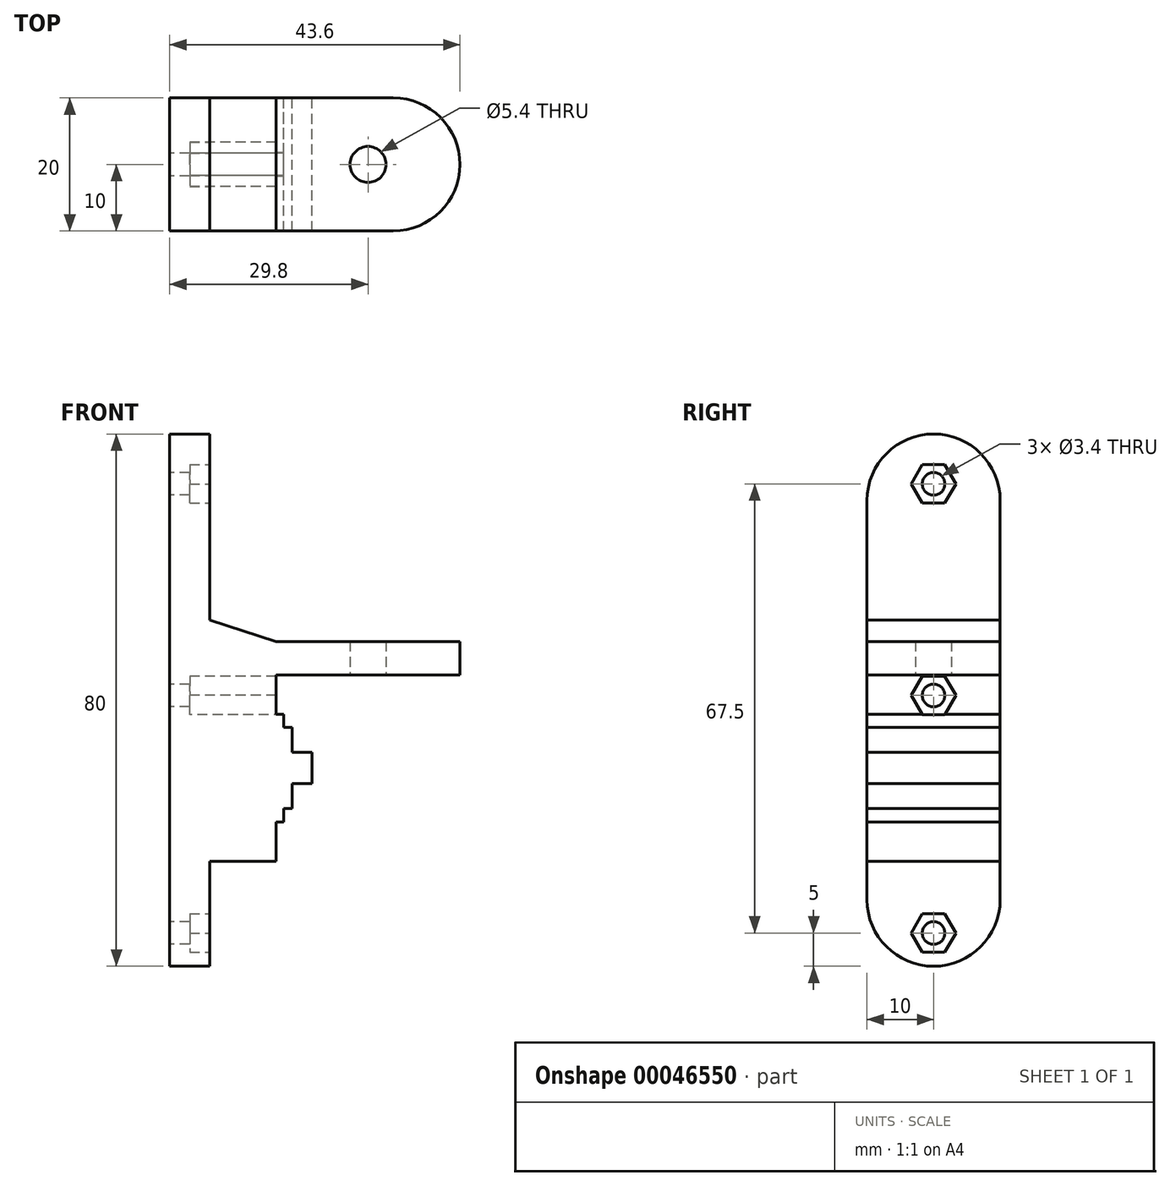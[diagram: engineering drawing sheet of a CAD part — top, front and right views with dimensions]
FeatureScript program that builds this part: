
annotation { "Feature Type Name" : "Feature", "Feature Type Description" : "" }
export const myFeature = defineFeature(function(context is Context, id is Id, definition is map)
    precondition{}
    {
        {
            var Q0;
            Q0=qCreatedBy(makeId("Front.planeOp"),FACE);
            var sketch = newSketch(context, id + "F0", { "sketchPlane" : qUnion([Q0])});
            skLineSegment(sketch, "E0", {"start": v(6, 12) * mm, "end": v(16, 8.8) * mm});
            skLineSegment(sketch, "E1", {"start": v(16, 8.8) * mm, "end": v(43.6, 8.8) * mm});
            skLineSegment(sketch, "E2", {"start": v(43.6, 8.8) * mm, "end": v(43.6, 3.8) * mm});
            skLineSegment(sketch, "E3", {"start": v(43.6, 3.8) * mm, "end": v(16, 3.8) * mm});
            skLineSegment(sketch, "E4", {"start": v(16, 3.8) * mm, "end": v(16, -2.1) * mm});
            skLineSegment(sketch, "E5", {"start": v(16, -2.1) * mm, "end": v(17.15, -2.1) * mm});
            skLineSegment(sketch, "E6", {"start": v(17.15, -2.1) * mm, "end": v(17.15, -4.1) * mm});
            skLineSegment(sketch, "E7", {"start": v(17.15, -4.1) * mm, "end": v(18.4, -4.1) * mm});
            skLineSegment(sketch, "E8", {"start": v(18.4, -4.1) * mm, "end": v(18.4, -7.85) * mm});
            skLineSegment(sketch, "E9", {"start": v(18.4, -7.85) * mm, "end": v(21.4, -7.85) * mm});
            skLineSegment(sketch, "E10", {"start": v(21.4, -7.85) * mm, "end": v(21.4, -12.55) * mm});
            skLineSegment(sketch, "E11", {"start": v(21.4, -12.55) * mm, "end": v(18.4, -12.55) * mm});
            skLineSegment(sketch, "E12", {"start": v(18.4, -12.55) * mm, "end": v(18.4, -16.3) * mm});
            skLineSegment(sketch, "E13", {"start": v(18.4, -16.3) * mm, "end": v(17.15, -16.3) * mm});
            skLineSegment(sketch, "E14", {"start": v(17.15, -16.3) * mm, "end": v(17.15, -18.3) * mm});
            skLineSegment(sketch, "E15", {"start": v(17.15, -18.3) * mm, "end": v(16, -18.3) * mm});
            skLineSegment(sketch, "E16", {"start": v(16, -18.3) * mm, "end": v(16, -24.2) * mm});
            skLineSegment(sketch, "E17", {"start": v(16, -24.2) * mm, "end": v(6, -24.2) * mm});
            skLineSegment(sketch, "E18", {"start": v(0, 40) * mm, "end": v(6, 40) * mm});
            skLineSegment(sketch, "E19", {"start": v(0, -40) * mm, "end": v(6, -40) * mm});
            skLineSegment(sketch, "E20", {"start": v(6, -40) * mm, "end": v(6, -24.2) * mm});
            skLineSegment(sketch, "E21", {"start": v(0, 40) * mm, "end": v(0, -40) * mm});
            skLineSegment(sketch, "E22", {"start": v(6, 40) * mm, "end": v(6, 12) * mm});
            skLineSegment(sketch, "E23", {"start": v(16, 8.8) * mm, "end": v(16, -24.2) * mm, "construction": true});
            skSolve(sketch);
        }
        {
            var Q0;
            Q0=qSketchRegion(id+"F0",true);
            extrude(context, id + "F1", {"entities" : qUnion([Q0]), "depth" : 20 * mm});
        }
        {
            var Q0;
            Q0=makeQuery(id+"F1.opExtrude","SWEPT_FACE",FACE,{"disambiguationData":[OSD([sQuery(id+"F0.wireOp",EDGE,"E3")])]});
            var sketch = newSketch(context, id + "F2", { "sketchPlane" : qUnion([Q0])});
            skLineSegment(sketch, "E24", {"start": v(43.6, 10) * mm, "end": v(16, 10) * mm, "construction": true});
            skLineSegment(sketch, "E25", {"start": v(29.8, 20) * mm, "end": v(29.8, 0) * mm, "construction": true});
            skCircle(sketch, "E26", {"center": v(29.8, 10) * mm, "radius": 2.7 * mm});
            skSolve(sketch);
        }
        {
            var Q0;
            Q0=makeQuery(id+"F2.imprint","IMPRINT",FACE,{"disambiguationData":[TD([[makeQuery(id+"F2.imprint","IMPRINT",EDGE,{"derivedFrom":sQuery(id+"F2.wireOp",EDGE,"E26")}),1.0]])]});
            var Q1;
            Q1=sQuery(id+"F2.wireOp",EDGE,"E26");
            extrude(context, id + "F3", {"entities" : qUnion([Q0]), "operationType" : NewBodyOperationType.REMOVE, "surfaceEntities" : qUnion([Q1]), "endBound" : BoundingType.UP_TO_NEXT, "oppositeDirection" : true, "depth" : 25 * mm});
        }
        {
            var Q0;
            Q0=makeQuery(id+"F1.opExtrude","SWEPT_FACE",FACE,{"disambiguationData":[OSD([sQuery(id+"F0.wireOp",EDGE,"E21")])]});
            var sketch = newSketch(context, id + "F4", { "sketchPlane" : qUnion([Q0])});
            skCircle(sketch, "E27", {"center": v(10, 32.5) * mm, "radius": 1.7 * mm});
            skCircle(sketch, "E28", {"center": v(10, 0.7) * mm, "radius": 1.7 * mm});
            skCircle(sketch, "E29", {"center": v(10, -35) * mm, "radius": 1.7 * mm});
            skLineSegment(sketch, "E30", {"start": v(10, 40) * mm, "end": v(10, -40) * mm, "construction": true});
            skSolve(sketch);
        }
        {
            var Q0;
            Q0=makeQuery(id+"F4.imprint","IMPRINT",FACE,{"disambiguationData":[TD([[makeQuery(id+"F4.imprint","IMPRINT",EDGE,{"derivedFrom":sQuery(id+"F4.wireOp",EDGE,"E27")}),1.0]])]});
            var Q1;
            Q1=makeQuery(id+"F4.imprint","IMPRINT",FACE,{"disambiguationData":[TD([[makeQuery(id+"F4.imprint","IMPRINT",EDGE,{"derivedFrom":sQuery(id+"F4.wireOp",EDGE,"E28")}),1.0]])]});
            var Q2;
            Q2=makeQuery(id+"F4.imprint","IMPRINT",FACE,{"disambiguationData":[TD([[makeQuery(id+"F4.imprint","IMPRINT",EDGE,{"derivedFrom":sQuery(id+"F4.wireOp",EDGE,"E29")}),1.0]])]});
            extrude(context, id + "F5", {"entities" : qUnion([Q0, Q1, Q2]), "operationType" : NewBodyOperationType.REMOVE, "endBound" : BoundingType.UP_TO_NEXT, "oppositeDirection" : true, "depth" : 25 * mm});
        }
        {
            var Q0;
            Q0=makeQuery(id+"F1.opExtrude","SWEPT_FACE",FACE,{"disambiguationData":[OSD([sQuery(id+"F0.wireOp",EDGE,"E22")])]});
            var sketch = newSketch(context, id + "F6", { "sketchPlane" : qUnion([Q0])});
            skCircle(sketch, "E31.0", {"center": v(-10, 32.5) * mm, "radius": 1.7 * mm});
            skCircle(sketch, "E32.cCircle", {"center": v(-10, 32.5) * mm, "radius": 2.9 * mm, "construction": true});
            skLineSegment(sketch, "E32.0", {"start": v(-11.67, 29.6) * mm, "end": v(-13.35, 32.5) * mm});
            skLineSegment(sketch, "E32.1", {"start": v(-13.35, 32.5) * mm, "end": v(-11.67, 35.4) * mm});
            skLineSegment(sketch, "E32.2", {"start": v(-11.67, 35.4) * mm, "end": v(-8.33, 35.4) * mm});
            skLineSegment(sketch, "E32.3", {"start": v(-8.33, 35.4) * mm, "end": v(-6.65, 32.5) * mm});
            skLineSegment(sketch, "E32.4", {"start": v(-6.65, 32.5) * mm, "end": v(-8.33, 29.6) * mm});
            skLineSegment(sketch, "E32.5", {"start": v(-8.33, 29.6) * mm, "end": v(-11.67, 29.6) * mm});
            skPoint(sketch, "E32.0.midPoint", {"position": v(-12.51, 31.05) * mm});
            skSolve(sketch);
        }
        {
            var Q0;
            Q0=makeQuery(id+"F1.opExtrude","SWEPT_FACE",FACE,{"disambiguationData":[OSD([sQuery(id+"F0.wireOp",EDGE,"E20")])]});
            var sketch = newSketch(context, id + "F7", { "sketchPlane" : qUnion([Q0])});
            skCircle(sketch, "E33.cCircle", {"center": v(-10, -35) * mm, "radius": 2.9 * mm, "construction": true});
            skLineSegment(sketch, "E33.0", {"start": v(-6.65, -35) * mm, "end": v(-8.33, -37.9) * mm});
            skLineSegment(sketch, "E33.1", {"start": v(-8.33, -37.9) * mm, "end": v(-11.67, -37.9) * mm});
            skLineSegment(sketch, "E33.2", {"start": v(-11.67, -37.9) * mm, "end": v(-13.35, -35) * mm});
            skLineSegment(sketch, "E33.3", {"start": v(-13.35, -35) * mm, "end": v(-11.67, -32.1) * mm});
            skLineSegment(sketch, "E33.4", {"start": v(-11.67, -32.1) * mm, "end": v(-8.33, -32.1) * mm});
            skLineSegment(sketch, "E33.5", {"start": v(-8.33, -32.1) * mm, "end": v(-6.65, -35) * mm});
            skPoint(sketch, "E33.0.midPoint", {"position": v(-7.49, -36.45) * mm});
            skSolve(sketch);
        }
        {
            var Q0;
            Q0=makeQuery(id+"F1.opExtrude","SWEPT_FACE",FACE,{"disambiguationData":[OSD([sQuery(id+"F0.wireOp",EDGE,"E4")])]});
            var sketch = newSketch(context, id + "F8", { "sketchPlane" : qUnion([Q0])});
            skCircle(sketch, "E34.cCircle", {"center": v(-10, 0.7) * mm, "radius": 2.9 * mm, "construction": true});
            skLineSegment(sketch, "E34.0", {"start": v(-11.67, -2.2) * mm, "end": v(-13.35, 0.7) * mm});
            skLineSegment(sketch, "E34.1", {"start": v(-13.35, 0.7) * mm, "end": v(-11.67, 3.6) * mm});
            skLineSegment(sketch, "E34.2", {"start": v(-11.67, 3.6) * mm, "end": v(-8.33, 3.6) * mm});
            skLineSegment(sketch, "E34.3", {"start": v(-8.33, 3.6) * mm, "end": v(-6.65, 0.7) * mm});
            skLineSegment(sketch, "E34.4", {"start": v(-6.65, 0.7) * mm, "end": v(-8.33, -2.2) * mm});
            skLineSegment(sketch, "E34.5", {"start": v(-8.33, -2.2) * mm, "end": v(-11.67, -2.2) * mm});
            skPoint(sketch, "E34.0.midPoint", {"position": v(-12.51, -0.75) * mm});
            skSolve(sketch);
        }
        {
            var Q0;
            Q0=makeQuery(id+"F6.imprint","IMPRINT",FACE,{"disambiguationData":[TD([[makeQuery(id+"F6.imprint","IMPRINT",EDGE,{"derivedFrom":sQuery(id+"F6.wireOp",EDGE,"E31.0")}),1.0]])]});
            var Q1;
            Q1=makeQuery(id+"F7.imprint","IMPRINT",FACE,{"disambiguationData":[TD([[makeQuery(id+"F7.imprint","IMPRINT",EDGE,{"derivedFrom":sQuery(id+"F7.wireOp",EDGE,"E33.0")}),-1.0]])]});
            extrude(context, id + "F9", {"entities" : qUnion([Q0, Q1]), "operationType" : NewBodyOperationType.REMOVE, "oppositeDirection" : true, "depth" : 3 * mm});
        }
        {
            var Q0;
            {var subQ6=sQuery(id+"F8.wireOp",EDGE,"E34.1");Q0=makeQuery(id+"F8.imprint","IMPRINT",FACE,{"disambiguationData":[TD([[makeQuery(id+"F8.imprint","IMPRINT",EDGE,{"derivedFrom":subQ6}),-1.0]])]});}
            var Q1;
            {var subQ5=sQuery(id+"F8.wireOp",EDGE,"E34.5");Q1=makeQuery(id+"F8.imprint","IMPRINT",FACE,{"disambiguationData":[TD([[makeQuery(id+"F8.imprint","IMPRINT",EDGE,{"derivedFrom":subQ5}),-1.0]])]});}
            var Q2;
            {var subQ5=sQuery(id+"F8.wireOp",EDGE,"E34.2");Q2=makeQuery(id+"F8.imprint","IMPRINT",FACE,{"disambiguationData":[TD([[makeQuery(id+"F8.imprint","IMPRINT",EDGE,{"derivedFrom":subQ5}),-1.0]])]});}
            var Q3;
            Q3=makeQuery(id+"F1.opExtrude","SWEPT_FACE",FACE,{"disambiguationData":[OSD([sQuery(id+"F0.wireOp",EDGE,"E10")])]});
            var Q4;
            Q4=makeQuery(id+"F9.boolean.opBoolean","COPY",FACE,{"derivedFrom":makeQuery(id+"F9.opExtrude","CAP_FACE",FACE,{"disambiguationData":[OSD([sQuery(id+"F6.wireOp",EDGE,"E31.0"),sQuery(id+"F6.wireOp",EDGE,"E32.0"),sQuery(id+"F6.wireOp",EDGE,"E32.1"),sQuery(id+"F6.wireOp",EDGE,"E32.2"),sQuery(id+"F6.wireOp",EDGE,"E32.3"),sQuery(id+"F6.wireOp",EDGE,"E32.4"),sQuery(id+"F6.wireOp",EDGE,"E32.5")])],"isStart":false})});
            extrude(context, id + "F10", {"entities" : qUnion([Q0, Q1, Q2]), "operationType" : NewBodyOperationType.REMOVE, "endBound" : BoundingType.UP_TO_SURFACE, "endBoundEntityFace" : qUnion([Q3]), "depth" : 25 * mm, "hasSecondDirection" : true, "secondDirectionBound" : SecondDirectionBoundingType.UP_TO_SURFACE, "secondDirectionOppositeDirection" : true, "secondDirectionBoundEntityFace" : qUnion([Q4]), "secondDirectionDepth" : 25 * mm});
        }
        {
            var Q0;
            Q0=makeQuery(id+"F1.opExtrude","CAP_EDGE",EDGE,{"disambiguationData":[OSD([sQuery(id+"F0.wireOp",EDGE,"E18")])],"isStart":false});
            var Q1;
            Q1=makeQuery(id+"F1.opExtrude","CAP_EDGE",EDGE,{"disambiguationData":[OSD([sQuery(id+"F0.wireOp",EDGE,"E18")])],"isStart":true});
            var Q2;
            Q2=makeQuery(id+"F1.opExtrude","CAP_EDGE",EDGE,{"disambiguationData":[OSD([sQuery(id+"F0.wireOp",EDGE,"E19")])],"isStart":false});
            var Q3;
            Q3=makeQuery(id+"F1.opExtrude","CAP_EDGE",EDGE,{"disambiguationData":[OSD([sQuery(id+"F0.wireOp",EDGE,"E19")])],"isStart":true});
            var Q4;
            Q4=makeQuery(id+"F1.opExtrude","CAP_EDGE",EDGE,{"disambiguationData":[OSD([sQuery(id+"F0.wireOp",EDGE,"E2")])],"isStart":true});
            var Q5;
            Q5=makeQuery(id+"F1.opExtrude","CAP_EDGE",EDGE,{"disambiguationData":[OSD([sQuery(id+"F0.wireOp",EDGE,"E2")])],"isStart":false});
            fillet(context, id + "F11", {"entities" : qUnion([Q0, Q1, Q2, Q3, Q4, Q5]), "radius" : 10 * mm, "tangentPropagation" : true, "allowEdgeOverflow" : false});
        }
    });
